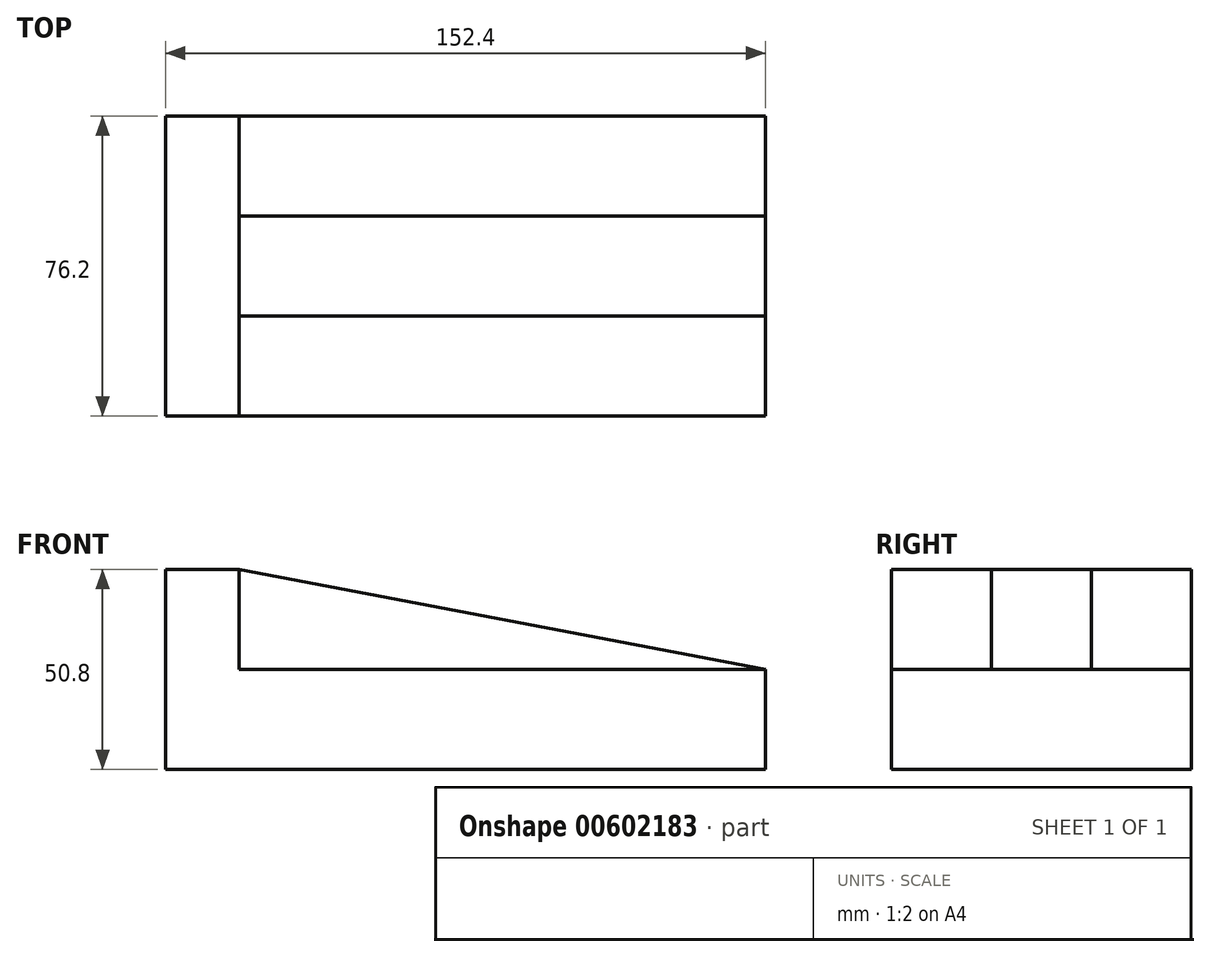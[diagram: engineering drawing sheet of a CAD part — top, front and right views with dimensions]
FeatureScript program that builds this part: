
annotation { "Feature Type Name" : "Feature", "Feature Type Description" : "" }
export const myFeature = defineFeature(function(context is Context, id is Id, definition is map)
    precondition{}
    {
        {
            var Q0;
            Q0=qCreatedBy(makeId("Front.planeOp"),FACE);
            var sketch = newSketch(context, id + "F0", { "sketchPlane" : qUnion([Q0])});
            skLineSegment(sketch, "E0", {"start": v(0, 0) * mm, "end": v(152.4, 0) * mm});
            skLineSegment(sketch, "E1", {"start": v(152.4, 0) * mm, "end": v(152.4, 50.8) * mm});
            skLineSegment(sketch, "E2", {"start": v(152.4, 50.8) * mm, "end": v(0, 50.8) * mm});
            skLineSegment(sketch, "E3", {"start": v(0, 50.8) * mm, "end": v(0, 0) * mm});
            skSolve(sketch);
        }
        {
            var Q0;
            Q0 = qSketchRegion(id + "F0", true);
            extrude(context, id + "F1", {"entities" : qUnion([Q0]), "oppositeDirection" : true, "depth" : 76.2 * mm, "offsetDistance" : 25.4 * mm});
        }
        {
            var Q0;
            Q0=makeQuery(id+"F1.opExtrude","SWEPT_FACE",FACE,{"disambiguationData":[OSD([sQuery(id+"F0.wireOp",EDGE,"E2")])]});
            var sketch = newSketch(context, id + "F2", { "sketchPlane" : qUnion([Q0])});
            skLineSegment(sketch, "E4", {"start": v(18.67, 0) * mm, "end": v(18.67, 76.2) * mm});
            skLineSegment(sketch, "E5", {"start": v(18.67, 50.8) * mm, "end": v(152.4, 50.8) * mm});
            skLineSegment(sketch, "E6", {"start": v(18.67, 25.4) * mm, "end": v(152.4, 25.4) * mm});
            skLineSegment(sketch, "E7", {"start": v(18.67, 50.8) * mm, "end": v(18.67, 76.2) * mm});
            skLineSegment(sketch, "E8", {"start": v(18.67, 0) * mm, "end": v(18.67, 25.4) * mm});
            skSolve(sketch);
        }
        {
            var Q0;
            {var subQ0=sQuery(id+"F2.wireOp",EDGE,"E6");Q0=makeQuery(id+"F2.imprint","IMPRINT",FACE,{"disambiguationData":[TD([[makeQuery(id+"F2.imprint","IMPRINT",EDGE,{"derivedFrom":subQ0}),-1.0]])]});}
            extrude(context, id + "F3", {"entities" : qUnion([Q0]), "operationType" : NewBodyOperationType.REMOVE, "oppositeDirection" : true, "depth" : 25.4 * mm, "offsetDistance" : 25.4 * mm});
        }
        {
            var Q0;
            Q0=makeQuery(id+"F1.opExtrude","SWEPT_FACE",FACE,{"disambiguationData":[OSD([sQuery(id+"F0.wireOp",EDGE,"E2")])]});
            var sketch = newSketch(context, id + "F4", { "sketchPlane" : qUnion([Q0])});
            skLineSegment(sketch, "E9", {"start": v(18.67, 25.4) * mm, "end": v(18.67, 76.2) * mm});
            skLineSegment(sketch, "E10", {"start": v(18.67, 50.8) * mm, "end": v(152.4, 50.8) * mm});
            skLineSegment(sketch, "E11", {"start": v(18.67, 50.8) * mm, "end": v(18.67, 76.2) * mm});
            skSolve(sketch);
        }
        {
            var Q0;
            {var subQ0=sQuery(id+"F4.wireOp",EDGE,"E10");Q0=makeQuery(id+"F4.imprint","IMPRINT",FACE,{"disambiguationData":[TD([[makeQuery(id+"F4.imprint","IMPRINT",EDGE,{"derivedFrom":subQ0}),1.0]])]});}
            extrude(context, id + "F5", {"entities" : qUnion([Q0]), "operationType" : NewBodyOperationType.REMOVE, "oppositeDirection" : true, "depth" : 25.4 * mm, "offsetDistance" : 25.4 * mm});
        }
        {
            var Q0;
            Q0=makeQuery(id+"F3.boolean.opBoolean","COPY",FACE,{"derivedFrom":makeQuery(id+"F3.opExtrude","SWEPT_FACE",FACE,{"disambiguationData":[OSD([sQuery(id+"F2.wireOp",EDGE,"E6")])]})});
            var sketch = newSketch(context, id + "F6", { "sketchPlane" : qUnion([Q0])});
            skLineSegment(sketch, "E12", {"start": v(18.67, 50.8) * mm, "end": v(152.4, 25.4) * mm});
            skLineSegment(sketch, "E13", {"start": v(152.4, 25.4) * mm, "end": v(152.4, 50.8) * mm});
            skLineSegment(sketch, "E14", {"start": v(152.4, 50.8) * mm, "end": v(18.67, 50.8) * mm});
            skSolve(sketch);
        }
        {
            var Q0;
            Q0 = qSketchRegion(id + "F6", true);
            extrude(context, id + "F7", {"entities" : qUnion([Q0]), "operationType" : NewBodyOperationType.REMOVE, "oppositeDirection" : true, "depth" : 25.4 * mm, "offsetDistance" : 25.4 * mm});
        }
    });
